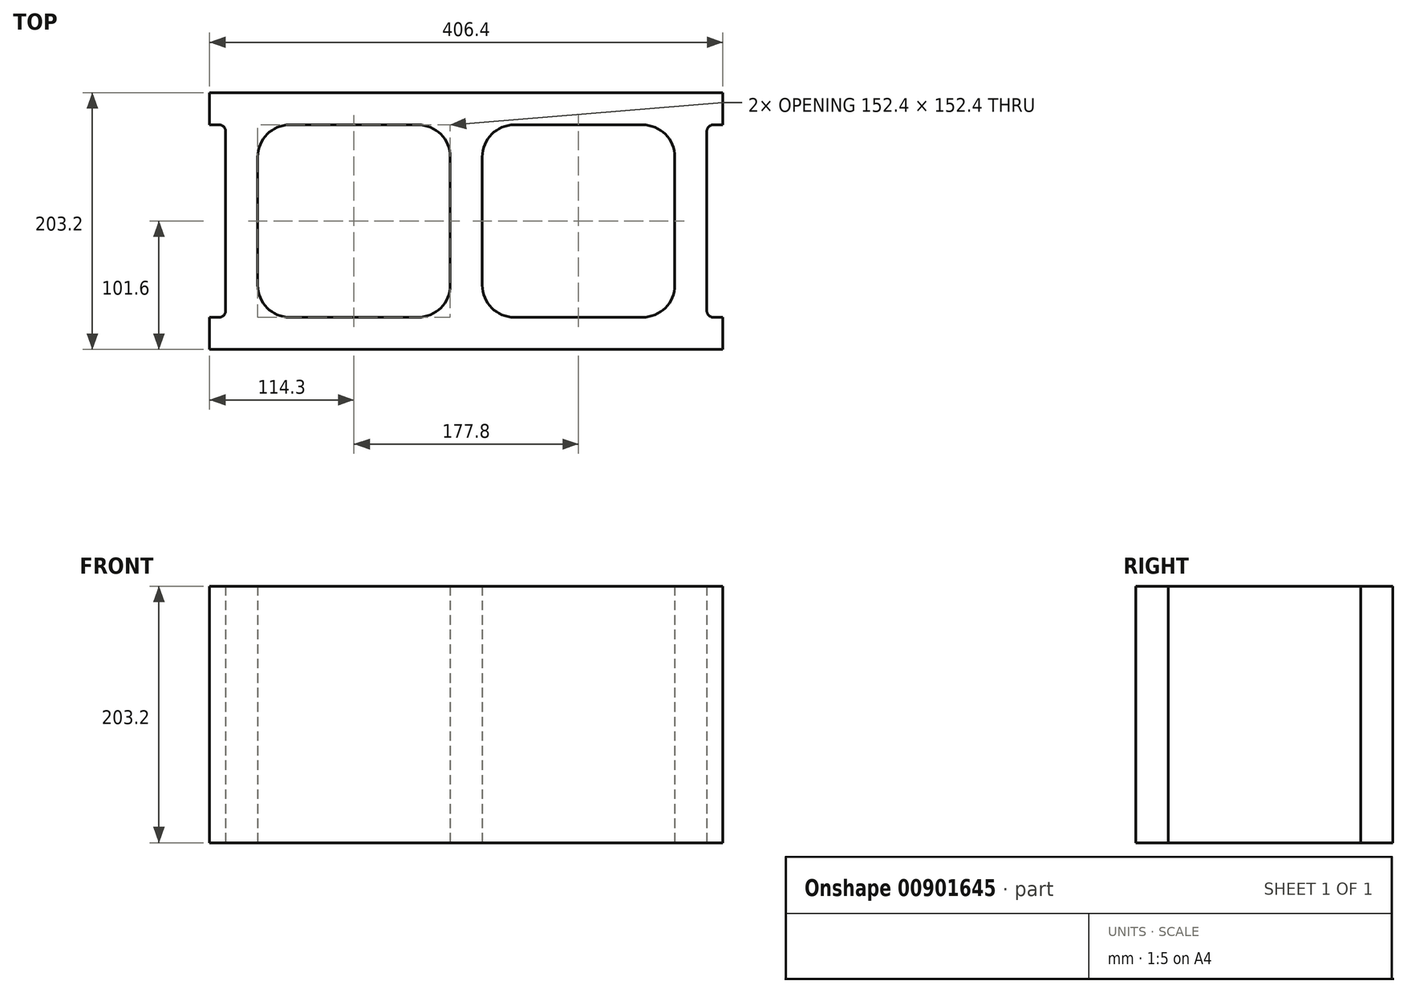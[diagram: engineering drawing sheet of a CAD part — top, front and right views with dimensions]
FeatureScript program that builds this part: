
annotation { "Feature Type Name" : "Feature", "Feature Type Description" : "" }
export const myFeature = defineFeature(function(context is Context, id is Id, definition is map)
    precondition{}
    {
        {
            var Q0;
            Q0=qCreatedBy(makeId("Top.planeOp"),FACE);
            var sketch = newSketch(context, id + "F0", { "sketchPlane" : qUnion([Q0])});
            skLineSegment(sketch, "E0.bottom", {"start": v(-203.2, 101.6) * mm, "end": v(203.2, 101.6) * mm});
            skLineSegment(sketch, "E0.top", {"start": v(-203.2, -101.6) * mm, "end": v(203.2, -101.6) * mm});
            skLineSegment(sketch, "E0.left", {"start": v(-203.2, 101.6) * mm, "end": v(-203.2, -101.6) * mm, "construction": true});
            skLineSegment(sketch, "E0.right", {"start": v(203.2, 101.6) * mm, "end": v(203.2, -101.6) * mm, "construction": true});
            skLineSegment(sketch, "E1.bottom", {"start": v(-165.1, 76.2) * mm, "end": v(-12.7, 76.2) * mm});
            skLineSegment(sketch, "E1.top", {"start": v(-165.1, -76.2) * mm, "end": v(-12.7, -76.2) * mm});
            skLineSegment(sketch, "E1.left", {"start": v(-165.1, 76.2) * mm, "end": v(-165.1, -76.2) * mm});
            skLineSegment(sketch, "E1.right", {"start": v(-12.7, 76.2) * mm, "end": v(-12.7, -76.2) * mm});
            skLineSegment(sketch, "E2.bottom", {"start": v(12.7, 76.2) * mm, "end": v(165.1, 76.2) * mm});
            skLineSegment(sketch, "E2.top", {"start": v(12.7, -76.2) * mm, "end": v(165.1, -76.2) * mm});
            skLineSegment(sketch, "E2.left", {"start": v(12.7, 76.2) * mm, "end": v(12.7, -76.2) * mm});
            skLineSegment(sketch, "E2.right", {"start": v(165.1, 76.2) * mm, "end": v(165.1, -76.2) * mm});
            skLineSegment(sketch, "E3.bottom", {"start": v(-203.2, 76.2) * mm, "end": v(-190.5, 76.2) * mm});
            skLineSegment(sketch, "E3.top", {"start": v(-203.2, -76.2) * mm, "end": v(-190.5, -76.2) * mm});
            skLineSegment(sketch, "E3.right", {"start": v(-190.5, 76.2) * mm, "end": v(-190.5, -76.2) * mm});
            skLineSegment(sketch, "E4.bottom", {"start": v(203.2, -76.2) * mm, "end": v(190.5, -76.2) * mm});
            skLineSegment(sketch, "E4.top", {"start": v(203.2, 76.2) * mm, "end": v(190.5, 76.2) * mm});
            skLineSegment(sketch, "E4.right", {"start": v(190.5, -76.2) * mm, "end": v(190.5, 76.2) * mm});
            skLineSegment(sketch, "E5", {"start": v(-190.5, 76.2) * mm, "end": v(-165.1, 76.2) * mm, "construction": true});
            skLineSegment(sketch, "E6", {"start": v(165.1, 76.2) * mm, "end": v(190.5, 76.2) * mm, "construction": true});
            skLineSegment(sketch, "E7", {"start": v(165.1, -76.2) * mm, "end": v(190.5, -76.2) * mm, "construction": true});
            skLineSegment(sketch, "E8", {"start": v(-190.5, -76.2) * mm, "end": v(-165.1, -76.2) * mm, "construction": true});
            skLineSegment(sketch, "E9", {"start": v(-203.2, 101.6) * mm, "end": v(-203.2, 76.2) * mm});
            skLineSegment(sketch, "E10", {"start": v(-203.2, -101.6) * mm, "end": v(-203.2, -76.2) * mm});
            skLineSegment(sketch, "E11", {"start": v(203.2, -101.6) * mm, "end": v(203.2, -76.2) * mm});
            skLineSegment(sketch, "E12", {"start": v(203.2, 76.2) * mm, "end": v(203.2, 101.6) * mm});
            skSolve(sketch);
        }
        {
            var Q0;
            Q0 = qSketchRegion(id + "F0", true);
            extrude(context, id + "F1", {"entities" : qUnion([Q0]), "depth" : 203.2 * mm, "offsetDistance" : 25 * mm});
        }
        {
            var Q0;
            Q0=makeQuery(id+"F1.opExtrude","SWEPT_EDGE",EDGE,{"disambiguationData":[OSD([sQuery(id+"F0.wireOp",EDGE,"E1.bottom"),sQuery(id+"F0.wireOp",EDGE,"E1.left")])]});
            var Q1;
            Q1=makeQuery(id+"F1.opExtrude","SWEPT_EDGE",EDGE,{"disambiguationData":[OSD([sQuery(id+"F0.wireOp",EDGE,"E1.top"),sQuery(id+"F0.wireOp",EDGE,"E1.left")])]});
            var Q2;
            Q2=makeQuery(id+"F1.opExtrude","SWEPT_EDGE",EDGE,{"disambiguationData":[OSD([sQuery(id+"F0.wireOp",EDGE,"E2.top"),sQuery(id+"F0.wireOp",EDGE,"E2.left")])]});
            var Q3;
            Q3=makeQuery(id+"F1.opExtrude","SWEPT_EDGE",EDGE,{"disambiguationData":[OSD([sQuery(id+"F0.wireOp",EDGE,"E2.bottom"),sQuery(id+"F0.wireOp",EDGE,"E2.left")])]});
            var Q4;
            Q4=makeQuery(id+"F1.opExtrude","SWEPT_EDGE",EDGE,{"disambiguationData":[OSD([sQuery(id+"F0.wireOp",EDGE,"E2.bottom"),sQuery(id+"F0.wireOp",EDGE,"E2.right")])]});
            var Q5;
            Q5=makeQuery(id+"F1.opExtrude","SWEPT_EDGE",EDGE,{"disambiguationData":[OSD([sQuery(id+"F0.wireOp",EDGE,"E2.top"),sQuery(id+"F0.wireOp",EDGE,"E2.right")])]});
            var Q6;
            Q6=makeQuery(id+"F1.opExtrude","SWEPT_EDGE",EDGE,{"disambiguationData":[OSD([sQuery(id+"F0.wireOp",EDGE,"E1.bottom"),sQuery(id+"F0.wireOp",EDGE,"E1.right")])]});
            var Q7;
            Q7=makeQuery(id+"F1.opExtrude","SWEPT_EDGE",EDGE,{"disambiguationData":[OSD([sQuery(id+"F0.wireOp",EDGE,"E1.top"),sQuery(id+"F0.wireOp",EDGE,"E1.right")])]});
            fillet(context, id + "F2", {"entities" : qUnion([Q0, Q1, Q2, Q3, Q4, Q5, Q6, Q7]), "radius" : 25.4 * mm, "tangentPropagation" : true, "allowEdgeOverflow" : false});
        }
        {
            var Q0;
            Q0=makeQuery(id+"F1.opExtrude","SWEPT_EDGE",EDGE,{"disambiguationData":[OSD([sQuery(id+"F0.wireOp",EDGE,"E3.bottom"),sQuery(id+"F0.wireOp",EDGE,"E3.right")])]});
            var Q1;
            Q1=makeQuery(id+"F1.opExtrude","SWEPT_EDGE",EDGE,{"disambiguationData":[OSD([sQuery(id+"F0.wireOp",EDGE,"E3.top"),sQuery(id+"F0.wireOp",EDGE,"E3.right")])]});
            var Q2;
            Q2=makeQuery(id+"F1.opExtrude","SWEPT_EDGE",EDGE,{"disambiguationData":[OSD([sQuery(id+"F0.wireOp",EDGE,"E4.top"),sQuery(id+"F0.wireOp",EDGE,"E4.right")])]});
            var Q3;
            Q3=makeQuery(id+"F1.opExtrude","SWEPT_EDGE",EDGE,{"disambiguationData":[OSD([sQuery(id+"F0.wireOp",EDGE,"E4.bottom"),sQuery(id+"F0.wireOp",EDGE,"E4.right")])]});
            fillet(context, id + "F3", {"entities" : qUnion([Q0, Q1, Q2, Q3]), "radius" : 5 * mm, "tangentPropagation" : true, "allowEdgeOverflow" : false});
        }
    });
